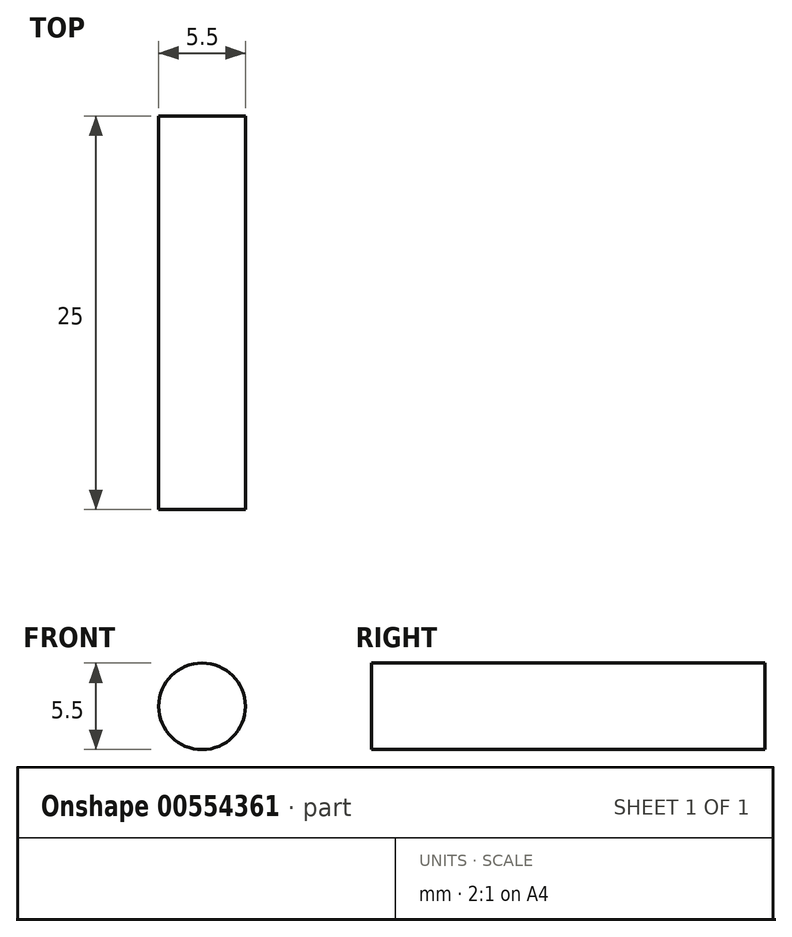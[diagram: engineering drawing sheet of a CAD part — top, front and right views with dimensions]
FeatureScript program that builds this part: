
annotation { "Feature Type Name" : "Feature", "Feature Type Description" : "" }
export const myFeature = defineFeature(function(context is Context, id is Id, definition is map)
    precondition{}
    {
        {
            var Q0;
            Q0=qCreatedBy(makeId("Front.planeOp"),FACE);
            var sketch = newSketch(context, id + "F0", { "sketchPlane" : qUnion([Q0])});
            skCircle(sketch, "E0", {"center": v(0, 0) * mm, "radius": 2.75 * mm});
            skSolve(sketch);
        }
        {
            var Q0;
            Q0 = qSketchRegion(id + "F0", true);
            extrude(context, id + "F1", {"entities" : qUnion([Q0]), "depth" : 25 * mm, "offsetDistance" : 25 * mm});
        }
    });
